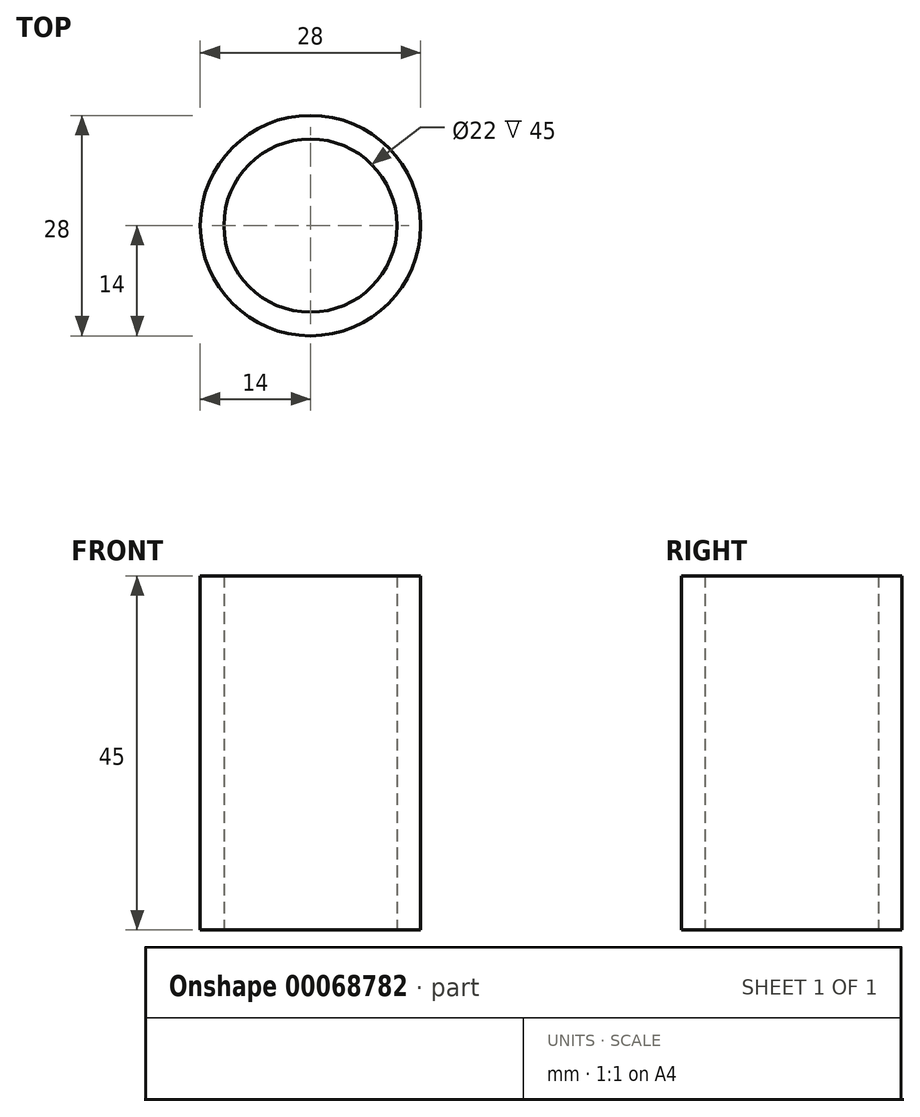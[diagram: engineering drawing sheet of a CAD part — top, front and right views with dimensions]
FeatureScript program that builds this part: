
annotation { "Feature Type Name" : "Feature", "Feature Type Description" : "" }
export const myFeature = defineFeature(function(context is Context, id is Id, definition is map)
    precondition{}
    {
        {
            var Q0;
            Q0=qCreatedBy(makeId("Top.planeOp"),FACE);
            var sketch = newSketch(context, id + "F0", { "sketchPlane" : qUnion([Q0])});
            skCircle(sketch, "E0", {"center": v(0, 0) * mm, "radius": 11 * mm});
            skCircle(sketch, "E1", {"center": v(0, 0) * mm, "radius": 14 * mm});
            skSolve(sketch);
        }
        {
            var Q0;
            Q0=makeQuery(id+"F0.imprint","IMPRINT",FACE,{"disambiguationData":[TD([[makeQuery(id+"F0.imprint","IMPRINT",EDGE,{"derivedFrom":sQuery(id+"F0.wireOp",EDGE,"E0")}),-1.0]])]});
            extrude(context, id + "F1", {"entities" : qUnion([Q0]), "depth" : 45 * mm});
        }
    });
